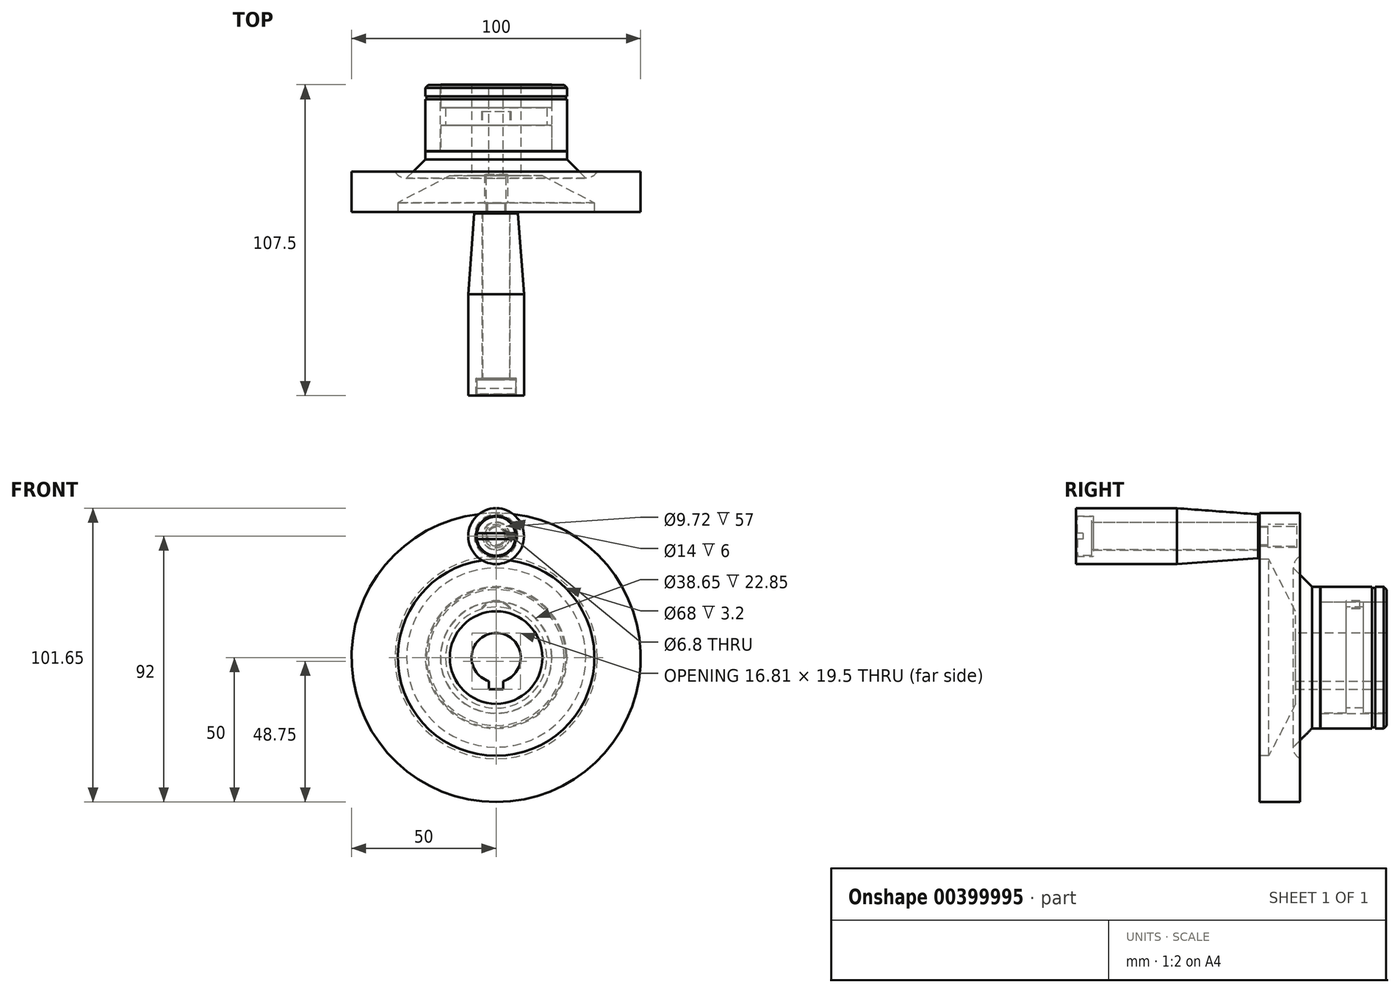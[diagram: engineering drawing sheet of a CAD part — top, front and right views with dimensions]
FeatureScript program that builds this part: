
annotation { "Feature Type Name" : "Feature", "Feature Type Description" : "" }
export const myFeature = defineFeature(function(context is Context, id is Id, definition is map)
    precondition{}
    {
        {
            var Q0;
            Q0=qCreatedBy(makeId("Right.planeOp"),FACE);
            var sketch = newSketch(context, id + "F0", { "sketchPlane" : qUnion([Q0])});
            skLineSegment(sketch, "E0", {"start": v(0, 8.5) * mm, "end": v(0, 19.2) * mm});
            skLineSegment(sketch, "E1", {"start": v(0, 19.2) * mm, "end": v(-8, 19.2) * mm});
            skLineSegment(sketch, "E2", {"start": v(-8, 19.2) * mm, "end": v(-8, 17.5) * mm});
            skLineSegment(sketch, "E3", {"start": v(-8, 17.5) * mm, "end": v(-14, 17.5) * mm});
            skLineSegment(sketch, "E4", {"start": v(-14, 17.5) * mm, "end": v(-14, 19.2) * mm});
            skLineSegment(sketch, "E5", {"start": v(-14, 19.2) * mm, "end": v(-23, 19.2) * mm});
            skLineSegment(sketch, "E6", {"start": v(-23, 19.2) * mm, "end": v(-23, 24.5) * mm});
            skLineSegment(sketch, "E7", {"start": v(-23, 24.5) * mm, "end": v(-25.8, 24.5) * mm});
            skLineSegment(sketch, "E8", {"start": v(-25.8, 24.5) * mm, "end": v(-32.3, 31) * mm});
            skLineSegment(sketch, "E9", {"start": v(-30, 35) * mm, "end": v(-30, 50) * mm});
            skLineSegment(sketch, "E10", {"start": v(-30, 50) * mm, "end": v(-44, 50) * mm});
            skLineSegment(sketch, "E11", {"start": v(-44, 50) * mm, "end": v(-44, 34) * mm});
            skLineSegment(sketch, "E12", {"start": v(-44, 34) * mm, "end": v(-40.8, 34) * mm});
            skLineSegment(sketch, "E13", {"start": v(-40.8, 34) * mm, "end": v(-31.5, 16) * mm});
            skLineSegment(sketch, "E14", {"start": v(-31.5, 16) * mm, "end": v(-31.5, 8.5) * mm});
            skLineSegment(sketch, "E15", {"start": v(-31.5, 8.5) * mm, "end": v(0, 8.5) * mm});
            skLineSegment(sketch, "E16", {"start": v(-31.5, 0) * mm, "end": v(0, 0) * mm, "construction": true});
            skArc(sketch, "E17", {"start": v(-30, 35) * mm, "mid": v(-31.68, 33.3) * mm, "end": v(-32.3, 31) * mm});
            skSolve(sketch);
        }
        {
            var Q0;
            Q0 = qSketchRegion(id + "F0", true);
            var Q1;
            Q1=sQuery(id+"F0.wireOp",EDGE,"E16");
            revolve(context, id + "F1", {"entities" : qUnion([Q0]), "axis" : qUnion([Q1]), "revolveType" : RevolveType.FULL});
        }
        {
            var Q0;
            Q0=makeQuery(id+"F1.opRevolve","SWEPT_FACE",FACE,{"disambiguationData":[OSD([sQuery(id+"F0.wireOp",EDGE,"E11")])]});
            var sketch = newSketch(context, id + "F2", { "sketchPlane" : qUnion([Q0])});
            skLineSegment(sketch, "E18", {"start": v(0, 50) * mm, "end": v(0, 34) * mm, "construction": true});
            skPoint(sketch, "E19", {"position": v(0, 42) * mm});
            skSolve(sketch);
        }
        {
            var Q0;
            Q0=sQuery(id+"F2.wireOp",VERTEX,"E19");
            var Q1;
            Q1=makeQuery(id+"F1.opRevolve","SWEPT_BODY",BODY,{"disambiguationData":[OSD([sQuery(id+"F0.wireOp",EDGE,"E0"),sQuery(id+"F0.wireOp",EDGE,"E1"),sQuery(id+"F0.wireOp",EDGE,"E2"),sQuery(id+"F0.wireOp",EDGE,"E3"),sQuery(id+"F0.wireOp",EDGE,"E4"),sQuery(id+"F0.wireOp",EDGE,"E5"),sQuery(id+"F0.wireOp",EDGE,"E6"),sQuery(id+"F0.wireOp",EDGE,"E7"),sQuery(id+"F0.wireOp",EDGE,"E8"),sQuery(id+"F0.wireOp",EDGE,"E9"),sQuery(id+"F0.wireOp",EDGE,"E10"),sQuery(id+"F0.wireOp",EDGE,"E11"),sQuery(id+"F0.wireOp",EDGE,"E12"),sQuery(id+"F0.wireOp",EDGE,"E13"),sQuery(id+"F0.wireOp",EDGE,"E14"),sQuery(id+"F0.wireOp",EDGE,"E15"),sQuery(id+"F0.wireOp",EDGE,"E17")])]});
            hole(context, id + "F3", {"style" : HoleStyle.SIMPLE, "endStyle" : HoleEndStyle.THROUGH, "standardTappedOrClearance" : lookupTablePath({ "standard" : "ISO", "engagement" : "75%", "pitch" : "1.25 mm", "size" : "M8", "type" : "Tapped" }), "standardBlindInLast" : lookupTablePath({ "standard" : "ISO", "engagement" : "75%", "pitch" : "1.25 mm", "size" : "M8", "type" : "Tapped" }), "holeDiameter" : 6.8 * mm, "showTappedDepth" : true, "isTappedThrough" : true, "tappedDepth" : 18 * mm, "tapClearance" : 3, "locations" : qUnion([Q0]), "scope" : qUnion([Q1]), "majorDiameter" : 8 * mm, "startStyle" : HoleStartStyle.SKETCH});
        }
        {
            var Q0;
            Q0=qCreatedBy(makeId("Front.planeOp"),FACE);
            var sketch = newSketch(context, id + "F4", { "sketchPlane" : qUnion([Q0])});
            skLineSegment(sketch, "E20.bottom", {"start": v(-2.5, -8.12) * mm, "end": v(2.5, -8.12) * mm});
            skLineSegment(sketch, "E20.top", {"start": v(-2.5, -11) * mm, "end": v(2.5, -11) * mm});
            skLineSegment(sketch, "E20.left", {"start": v(-2.5, -11) * mm, "end": v(-2.5, -8.12) * mm});
            skLineSegment(sketch, "E20.right", {"start": v(2.5, -11) * mm, "end": v(2.5, -8.12) * mm});
            skSolve(sketch);
        }
        {
            var Q0;
            Q0=makeQuery(id+"F4.imprint","IMPRINT",FACE,{"disambiguationData":[TD([[makeQuery(id+"F4.imprint","IMPRINT",EDGE,{"derivedFrom":sQuery(id+"F4.wireOp",EDGE,"E20.bottom")}),-1.0]])]});
            var Q1;
            Q1=makeQuery(id+"F1.opRevolve","SWEPT_FACE",FACE,{"disambiguationData":[OSD([sQuery(id+"F0.wireOp",EDGE,"E14")])]});
            extrude(context, id + "F5", {"entities" : qUnion([Q0]), "operationType" : NewBodyOperationType.REMOVE, "endBound" : BoundingType.UP_TO_SURFACE, "endBoundEntityFace" : qUnion([Q1]), "depth" : 25 * mm});
        }
        {
            var Q0;
            Q0=qCreatedBy(makeId("Right.planeOp"),FACE);
            var sketch = newSketch(context, id + "F6", { "sketchPlane" : qUnion([Q0])});
            skLineSegment(sketch, "E21.bottom", {"start": v(-22.9, 19.32) * mm, "end": v(-0.05, 19.32) * mm});
            skLineSegment(sketch, "E21.top", {"start": v(-22.9, 24.5) * mm, "end": v(-5.05, 24.5) * mm});
            skLineSegment(sketch, "E21.left", {"start": v(-22.9, 19.32) * mm, "end": v(-22.9, 24.5) * mm});
            skLineSegment(sketch, "E21.right", {"start": v(-0.05, 19.32) * mm, "end": v(-0.05, 23.5) * mm});
            skLineSegment(sketch, "E22", {"start": v(-3.95, 24.5) * mm, "end": v(-3.95, 24.12) * mm});
            skLineSegment(sketch, "E23", {"start": v(-3.95, 24.12) * mm, "end": v(-5.05, 24.12) * mm});
            skLineSegment(sketch, "E24", {"start": v(-5.05, 24.12) * mm, "end": v(-5.05, 24.5) * mm});
            skLineSegment(sketch, "E25.trimOffspring", {"start": v(-3.95, 24.5) * mm, "end": v(-1.05, 24.5) * mm});
            skLineSegment(sketch, "E26", {"start": v(-1.05, 24.5) * mm, "end": v(-0.05, 23.5) * mm});
            skLineSegment(sketch, "E27", {"start": v(0, 0) * mm, "end": v(-22.9, 0) * mm, "construction": true});
            skSolve(sketch);
        }
        {
            var Q0;
            Q0 = qSketchRegion(id + "F6", true);
            var Q1;
            Q1=sQuery(id+"F6.wireOp",EDGE,"E27");
            revolve(context, id + "F7", {"entities" : qUnion([Q0]), "axis" : qUnion([Q1]), "revolveType" : RevolveType.FULL});
        }
        {
            var Q0;
            Q0=makeQuery(id+"F1.opRevolve","SWEPT_FACE",FACE,{"disambiguationData":[OSD([sQuery(id+"F0.wireOp",EDGE,"E4")])]});
            var sketch = newSketch(context, id + "F8", { "sketchPlane" : qUnion([Q0])});
            skArc(sketch, "E28", {"start": v(-4.77, 16.84) * mm, "mid": v(0, 19.3) * mm, "end": v(4.77, 16.84) * mm});
            skArc(sketch, "E29.0", {"start": v(-5.1, 17.07) * mm, "mid": v(0, 19.7) * mm, "end": v(5.1, 17.07) * mm});
            skLineSegment(sketch, "E30", {"start": v(5.1, 17.07) * mm, "end": v(4.77, 16.84) * mm});
            skLineSegment(sketch, "E31", {"start": v(-4.77, 16.84) * mm, "end": v(-5.1, 17.07) * mm});
            skLineSegment(sketch, "E32", {"start": v(-4.77, 16.84) * mm, "end": v(0, 13.44) * mm, "construction": true});
            skLineSegment(sketch, "E33", {"start": v(4.77, 16.84) * mm, "end": v(0, 13.44) * mm, "construction": true});
            skSolve(sketch);
        }
        {
            var Q0;
            Q0 = qSketchRegion(id + "F8", true);
            extrude(context, id + "F9", {"entities" : qUnion([Q0]), "depth" : 4.75 * mm});
        }
        {
            var Q0;
            Q0=qCreatedBy(makeId("Right.planeOp"),FACE);
            var sketch = newSketch(context, id + "F10", { "sketchPlane" : qUnion([Q0])});
            skLineSegment(sketch, "E34.bottom", {"start": v(-107, 48.75) * mm, "end": v(-102, 48.75) * mm});
            skLineSegment(sketch, "E34.top", {"start": v(-107, 35.25) * mm, "end": v(-102, 35.25) * mm});
            skLineSegment(sketch, "E34.left", {"start": v(-107, 48.75) * mm, "end": v(-107, 35.25) * mm});
            skLineSegment(sketch, "E34.right", {"start": v(-102, 48.75) * mm, "end": v(-102, 46.65) * mm});
            skLineSegment(sketch, "E35.bottom", {"start": v(-102, 46.65) * mm, "end": v(-44, 46.65) * mm});
            skLineSegment(sketch, "E35.top", {"start": v(-102, 37.35) * mm, "end": v(-44, 37.35) * mm});
            skLineSegment(sketch, "E35.right", {"start": v(-44, 46.65) * mm, "end": v(-44, 45) * mm});
            skLineSegment(sketch, "E36.bottom", {"start": v(-41, 46) * mm, "end": v(-31, 46) * mm});
            skLineSegment(sketch, "E36.top", {"start": v(-41, 38) * mm, "end": v(-31, 38) * mm});
            skLineSegment(sketch, "E36.right", {"start": v(-31, 46) * mm, "end": v(-31, 38) * mm});
            skLineSegment(sketch, "E37", {"start": v(-107, 42) * mm, "end": v(-31, 42) * mm});
            skLineSegment(sketch, "E38.trimOffspring", {"start": v(-102, 37.35) * mm, "end": v(-102, 35.25) * mm});
            skLineSegment(sketch, "E39", {"start": v(-44, 37.35) * mm, "end": v(-44, 39) * mm});
            skLineSegment(sketch, "E40", {"start": v(-41, 46) * mm, "end": v(-41, 45) * mm});
            skLineSegment(sketch, "E41", {"start": v(-41, 45) * mm, "end": v(-44, 45) * mm});
            skLineSegment(sketch, "E42", {"start": v(-41, 38) * mm, "end": v(-41, 39) * mm});
            skLineSegment(sketch, "E43", {"start": v(-41, 39) * mm, "end": v(-44, 39) * mm});
            skSolve(sketch);
        }
        {
            var Q0;
            {var subQ1=sQuery(id+"F10.wireOp",EDGE,"E34.bottom");Q0=makeQuery(id+"F10.imprint","IMPRINT",FACE,{"disambiguationData":[TD([[makeQuery(id+"F10.imprint","IMPRINT",EDGE,{"derivedFrom":subQ1}),-1.0]])]});}
            var Q1;
            Q1=sQuery(id+"F10.wireOp",EDGE,"E37");
            revolve(context, id + "F11", {"entities" : qUnion([Q0]), "axis" : qUnion([Q1]), "revolveType" : RevolveType.FULL});
        }
        {
            var Q0;
            Q0=makeQuery(id+"F11.opRevolve","SWEPT_FACE",FACE,{"disambiguationData":[OSD([sQuery(id+"F10.wireOp",EDGE,"E34.left")])]});
            var sketch = newSketch(context, id + "F12", { "sketchPlane" : qUnion([Q0])});
            skLineSegment(sketch, "E44.bottom", {"start": v(-6.75, 43) * mm, "end": v(6.75, 43) * mm});
            skLineSegment(sketch, "E44.top", {"start": v(-6.75, 41) * mm, "end": v(6.75, 41) * mm});
            skLineSegment(sketch, "E44.left", {"start": v(-6.75, 43) * mm, "end": v(-6.75, 41) * mm});
            skLineSegment(sketch, "E44.right", {"start": v(6.75, 43) * mm, "end": v(6.75, 41) * mm});
            skLineSegment(sketch, "E45", {"start": v(-6.75, 42) * mm, "end": v(6.75, 42) * mm, "construction": true});
            skSolve(sketch);
        }
        {
            var Q0;
            Q0 = qSketchRegion(id + "F12", true);
            extrude(context, id + "F13", {"entities" : qUnion([Q0]), "operationType" : NewBodyOperationType.REMOVE, "oppositeDirection" : true, "depth" : 2 * mm});
        }
        {
            var Q0;
            Q0=qCreatedBy(makeId("Right.planeOp"),FACE);
            var sketch = newSketch(context, id + "F14", { "sketchPlane" : qUnion([Q0])});
            skLineSegment(sketch, "E46", {"start": v(-101.5, 46.86) * mm, "end": v(-101.5, 49) * mm});
            skLineSegment(sketch, "E47", {"start": v(-101.5, 49) * mm, "end": v(-107.5, 49) * mm});
            skLineSegment(sketch, "E48", {"start": v(-107.5, 49) * mm, "end": v(-107.5, 51.65) * mm});
            skLineSegment(sketch, "E49", {"start": v(-107.5, 51.65) * mm, "end": v(-72.5, 51.65) * mm});
            skLineSegment(sketch, "E50", {"start": v(-72.5, 51.65) * mm, "end": v(-44.5, 49.56) * mm});
            skLineSegment(sketch, "E51", {"start": v(-44.5, 49.56) * mm, "end": v(-44.5, 46.86) * mm});
            skLineSegment(sketch, "E52", {"start": v(-44.5, 46.86) * mm, "end": v(-101.5, 46.86) * mm});
            skLineSegment(sketch, "E53", {"start": v(-44.5, 42) * mm, "end": v(-101.5, 42) * mm, "construction": true});
            skSolve(sketch);
        }
        {
            var Q0;
            Q0=makeQuery(id+"F14.imprint","IMPRINT",FACE,{"disambiguationData":[TD([[makeQuery(id+"F14.imprint","IMPRINT",EDGE,{"derivedFrom":sQuery(id+"F14.wireOp",EDGE,"E46")}),-1.0]])]});
            var Q1;
            Q1=sQuery(id+"F14.wireOp",EDGE,"E53");
            revolve(context, id + "F15", {"entities" : qUnion([Q0]), "axis" : qUnion([Q1]), "revolveType" : RevolveType.FULL});
        }
    });
